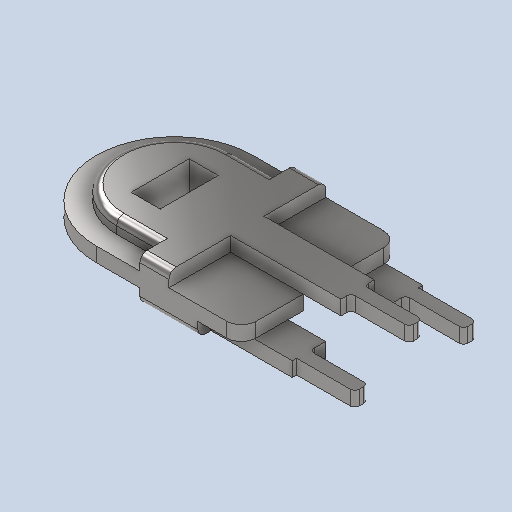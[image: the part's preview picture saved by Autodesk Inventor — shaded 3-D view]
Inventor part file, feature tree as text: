
AUTODESK INVENTOR PART (.ipt)
format: ipt  version: 2024.2 (Build 282272000, 272)  size: 439,808 bytes
history: native  units: mm
features: extrude x4, fillet x3, other x1, sketch x1
ambient origin geometry x8: Origin, YZ Plane, XZ Plane, XY Plane, X Axis, Y Axis, Z Axis, Center Point
bodies: Body1 (feature_tree)
feature tree (9):
  other  "Bryła1"
  sketch  "Szkic1"
  extrude  "Wyciągnięcie proste1"  Depth=10.8mm
  extrude  "Wyciągnięcie proste2"  Depth=18.0mm
  extrude  "Wyciągnięcie proste3"  Depth=4.0mm
  extrude  "Wyciągnięcie proste4"  Depth=0.9mm
  fillet  "Zaokrąglenie1"  Radius=7.5mm
  fillet  "Zaokrąglenie2"  Radius=2.3mm
  fillet  "Zaokrąglenie3"  Radius=0.3mm
